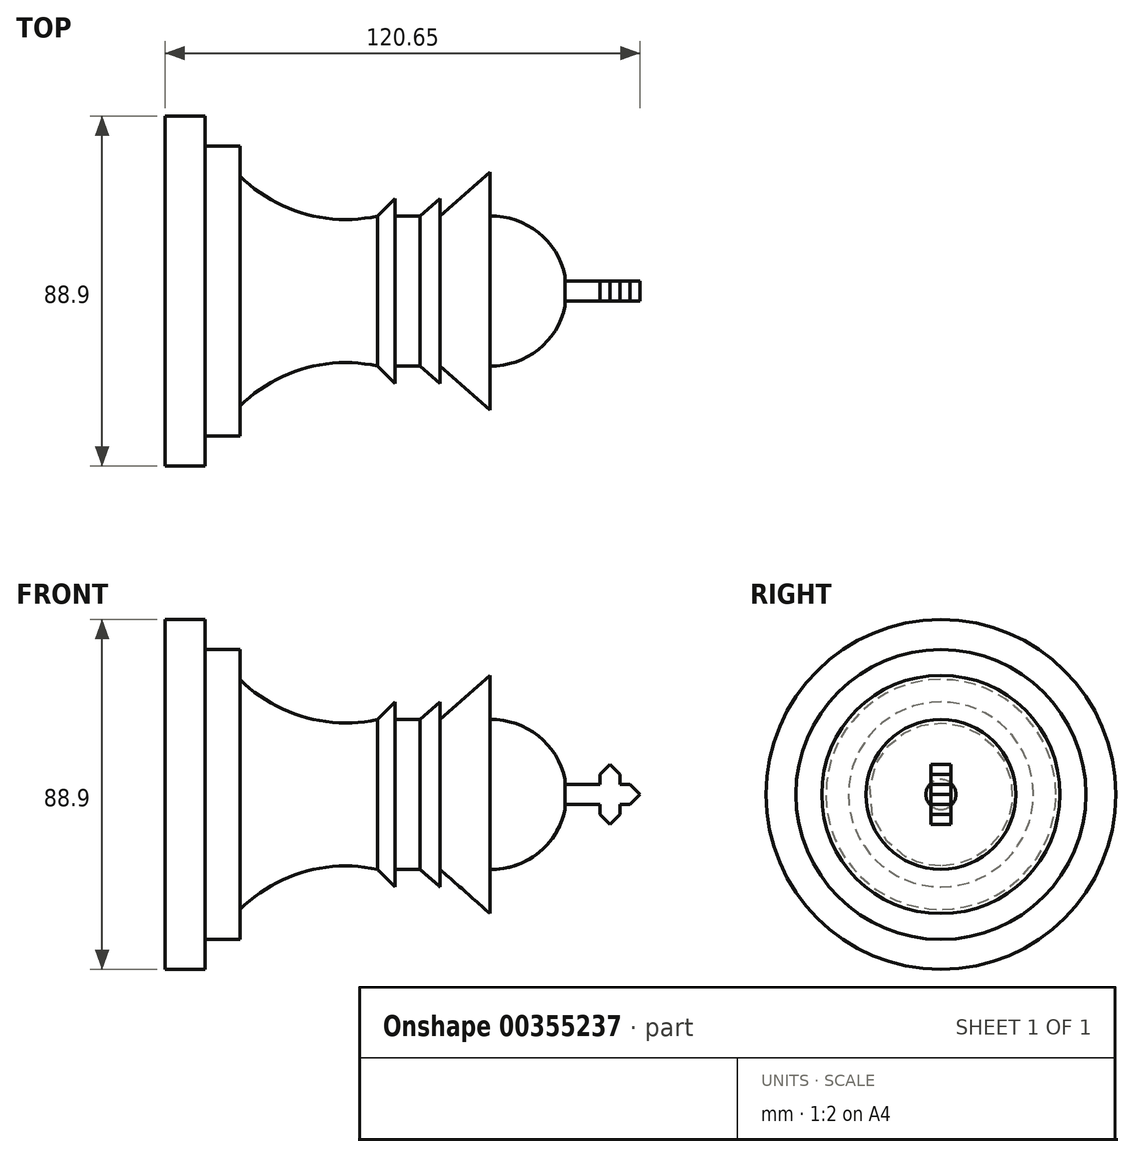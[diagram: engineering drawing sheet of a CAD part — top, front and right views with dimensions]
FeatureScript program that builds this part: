
annotation { "Feature Type Name" : "Feature", "Feature Type Description" : "" }
export const myFeature = defineFeature(function(context is Context, id is Id, definition is map)
    precondition{}
    {
        {
            var Q0;
            Q0=qCreatedBy(makeId("Front.planeOp"),FACE);
            var sketch = newSketch(context, id + "F0", { "sketchPlane" : qUnion([Q0])});
            skLineSegment(sketch, "E0", {"start": v(-19.05, 0) * mm, "end": v(-120.65, 0) * mm});
            skLineSegment(sketch, "E1", {"start": v(-120.65, 0) * mm, "end": v(-120.65, 44.45) * mm});
            skLineSegment(sketch, "E2", {"start": v(-120.65, 44.45) * mm, "end": v(-110.5, 44.45) * mm});
            skLineSegment(sketch, "E3", {"start": v(-110.5, 44.45) * mm, "end": v(-110.5, 36.83) * mm});
            skLineSegment(sketch, "E4", {"start": v(-110.5, 36.83) * mm, "end": v(-101.6, 36.83) * mm});
            skLineSegment(sketch, "E5", {"start": v(-101.6, 36.83) * mm, "end": v(-101.6, 29.2) * mm});
            skArc(sketch, "E6", {"start": v(-101.6, 29.2) * mm, "mid": v(-85.43, 19.69) * mm, "end": v(-66.68, 19.05) * mm});
            skLineSegment(sketch, "E7", {"start": v(-66.68, 19.05) * mm, "end": v(-62.23, 23.5) * mm});
            skLineSegment(sketch, "E8", {"start": v(-62.23, 23.5) * mm, "end": v(-62.23, 19.05) * mm});
            skLineSegment(sketch, "E9", {"start": v(-62.23, 19.05) * mm, "end": v(-55.88, 19.05) * mm});
            skLineSegment(sketch, "E10", {"start": v(-55.88, 19.05) * mm, "end": v(-50.8, 23.5) * mm});
            skLineSegment(sketch, "E11", {"start": v(-50.8, 23.5) * mm, "end": v(-50.8, 19.05) * mm});
            skLineSegment(sketch, "E12", {"start": v(-50.8, 19.05) * mm, "end": v(-38.1, 30.27) * mm});
            skLineSegment(sketch, "E13", {"start": v(-38.1, 30.27) * mm, "end": v(-38.1, 19.05) * mm});
            skLineSegment(sketch, "E14", {"start": v(-19.05, 0) * mm, "end": v(-19.05, 3.8) * mm});
            skArc(sketch, "E15", {"start": v(-19.05, 3.81) * mm, "mid": v(-25.82, 14.88) * mm, "end": v(-38.1, 19.05) * mm});
            skLineSegment(sketch, "E16", {"start": v(-19.05, 2.54) * mm, "end": v(0, 2.54) * mm});
            skLineSegment(sketch, "E17", {"start": v(0, 2.54) * mm, "end": v(0, -2.54) * mm});
            skLineSegment(sketch, "E18", {"start": v(0, -2.54) * mm, "end": v(-19.05, -2.54) * mm});
            skLineSegment(sketch, "E19", {"start": v(-19.05, -2.54) * mm, "end": v(-19.05, 2.54) * mm});
            skLineSegment(sketch, "E20.bottom", {"start": v(-10.16, 7.62) * mm, "end": v(-5.08, 7.62) * mm});
            skLineSegment(sketch, "E20.top", {"start": v(-10.16, -7.62) * mm, "end": v(-5.08, -7.62) * mm});
            skLineSegment(sketch, "E20.left", {"start": v(-10.16, 7.62) * mm, "end": v(-10.16, -7.62) * mm});
            skLineSegment(sketch, "E20.right", {"start": v(-5.08, 7.62) * mm, "end": v(-5.08, -7.62) * mm});
            skSolve(sketch);
        }
        {
            var Q0;
            Q0=makeQuery(id+"F0.imprint","IMPRINT",FACE,{"disambiguationData":[TD([[makeQuery(id+"F0.imprint","IMPRINT",EDGE,{"derivedFrom":sQuery(id+"F0.wireOp",EDGE,"E0")}),-1.0]])]});
            var Q1;
            Q1=sQuery(id+"F0.wireOp",EDGE,"E0");
            revolve(context, id + "F1", {"entities" : qUnion([Q0]), "axis" : qUnion([Q1]), "revolveType" : RevolveType.FULL});
        }
        {
            var Q0;
            {var subQ0=sQuery(id+"F0.wireOp",EDGE,"E17");Q0=makeQuery(id+"F0.imprint","IMPRINT",FACE,{"disambiguationData":[TD([[makeQuery(id+"F0.imprint","IMPRINT",EDGE,{"derivedFrom":subQ0}),-1.0]])]});}
            var Q1;
            {var subQ5=sQuery(id+"F0.wireOp",EDGE,"E20.top");Q1=makeQuery(id+"F0.imprint","IMPRINT",FACE,{"disambiguationData":[TD([[makeQuery(id+"F0.imprint","IMPRINT",EDGE,{"derivedFrom":subQ5}),1.0]])]});}
            var Q2;
            {var subQ0=sQuery(id+"F0.wireOp",EDGE,"E20.left");var subQ1=sQuery(id+"F0.wireOp",EDGE,"E16");var subQ2=makeQuery(id+"F0.imprint","INTERSECT",VERTEX,{"derivedFrom":[subQ1,subQ0]});Q2=makeQuery(id+"F0.imprint","IMPRINT",FACE,{"disambiguationData":[TD([[makeQuery(id+"F0.imprint","IMPRINT",EDGE,{"disambiguationData":[TD([[subQ2,-1.0]])],"derivedFrom":subQ1}),-1.0]])]});}
            var Q3;
            {var subQ5=sQuery(id+"F0.wireOp",EDGE,"E20.bottom");Q3=makeQuery(id+"F0.imprint","IMPRINT",FACE,{"disambiguationData":[TD([[makeQuery(id+"F0.imprint","IMPRINT",EDGE,{"derivedFrom":subQ5}),-1.0]])]});}
            var Q4;
            {var subQ0=sQuery(id+"F0.wireOp",EDGE,"E19");var subQ4=sQuery(id+"F0.wireOp",EDGE,"E18");var subQ5=makeQuery(id+"F0.imprint","INTERSECT",VERTEX,{"derivedFrom":[subQ4,subQ0]});Q4=makeQuery(id+"F0.imprint","IMPRINT",FACE,{"disambiguationData":[TD([[makeQuery(id+"F0.imprint","IMPRINT",EDGE,{"disambiguationData":[TD([[subQ5,1.0]])],"derivedFrom":subQ4}),-1.0]])]});}
            extrude(context, id + "F2", {"entities" : qUnion([Q0, Q1, Q2, Q3, Q4]), "operationType" : NewBodyOperationType.ADD, "depth" : 2.54 * mm, "hasSecondDirection" : true, "secondDirectionOppositeDirection" : true, "secondDirectionDepth" : 2.54 * mm});
        }
        {
            var Q0;
            Q0=makeQuery(id+"F2.opExtrude","SWEPT_EDGE",EDGE,{"disambiguationData":[OSD([sQuery(id+"F0.wireOp",EDGE,"E20.bottom"),sQuery(id+"F0.wireOp",EDGE,"E20.left")])]});
            var Q1;
            Q1=makeQuery(id+"F2.opExtrude","SWEPT_EDGE",EDGE,{"disambiguationData":[OSD([sQuery(id+"F0.wireOp",EDGE,"E20.bottom"),sQuery(id+"F0.wireOp",EDGE,"E20.right")])]});
            var Q2;
            Q2=makeQuery(id+"F2.opExtrude","SWEPT_EDGE",EDGE,{"disambiguationData":[OSD([sQuery(id+"F0.wireOp",EDGE,"E16"),sQuery(id+"F0.wireOp",EDGE,"E17")])]});
            var Q3;
            Q3=makeQuery(id+"F2.opExtrude","SWEPT_EDGE",EDGE,{"disambiguationData":[OSD([sQuery(id+"F0.wireOp",EDGE,"E17"),sQuery(id+"F0.wireOp",EDGE,"E18")])]});
            var Q4;
            Q4=makeQuery(id+"F2.opExtrude","SWEPT_EDGE",EDGE,{"disambiguationData":[OSD([sQuery(id+"F0.wireOp",EDGE,"E20.top"),sQuery(id+"F0.wireOp",EDGE,"E20.right")])]});
            var Q5;
            Q5=makeQuery(id+"F2.opExtrude","SWEPT_EDGE",EDGE,{"disambiguationData":[OSD([sQuery(id+"F0.wireOp",EDGE,"E20.top"),sQuery(id+"F0.wireOp",EDGE,"E20.left")])]});
            chamfer(context, id + "F3", {"entities" : qUnion([Q0, Q1, Q2, Q3, Q4, Q5]), "chamferType" : ChamferType.TWO_OFFSETS, "width1" : 2.54 * mm, "oppositeDirection" : false, "width2" : 2.54 * mm, "tangentPropagation" : true});
        }
    });
